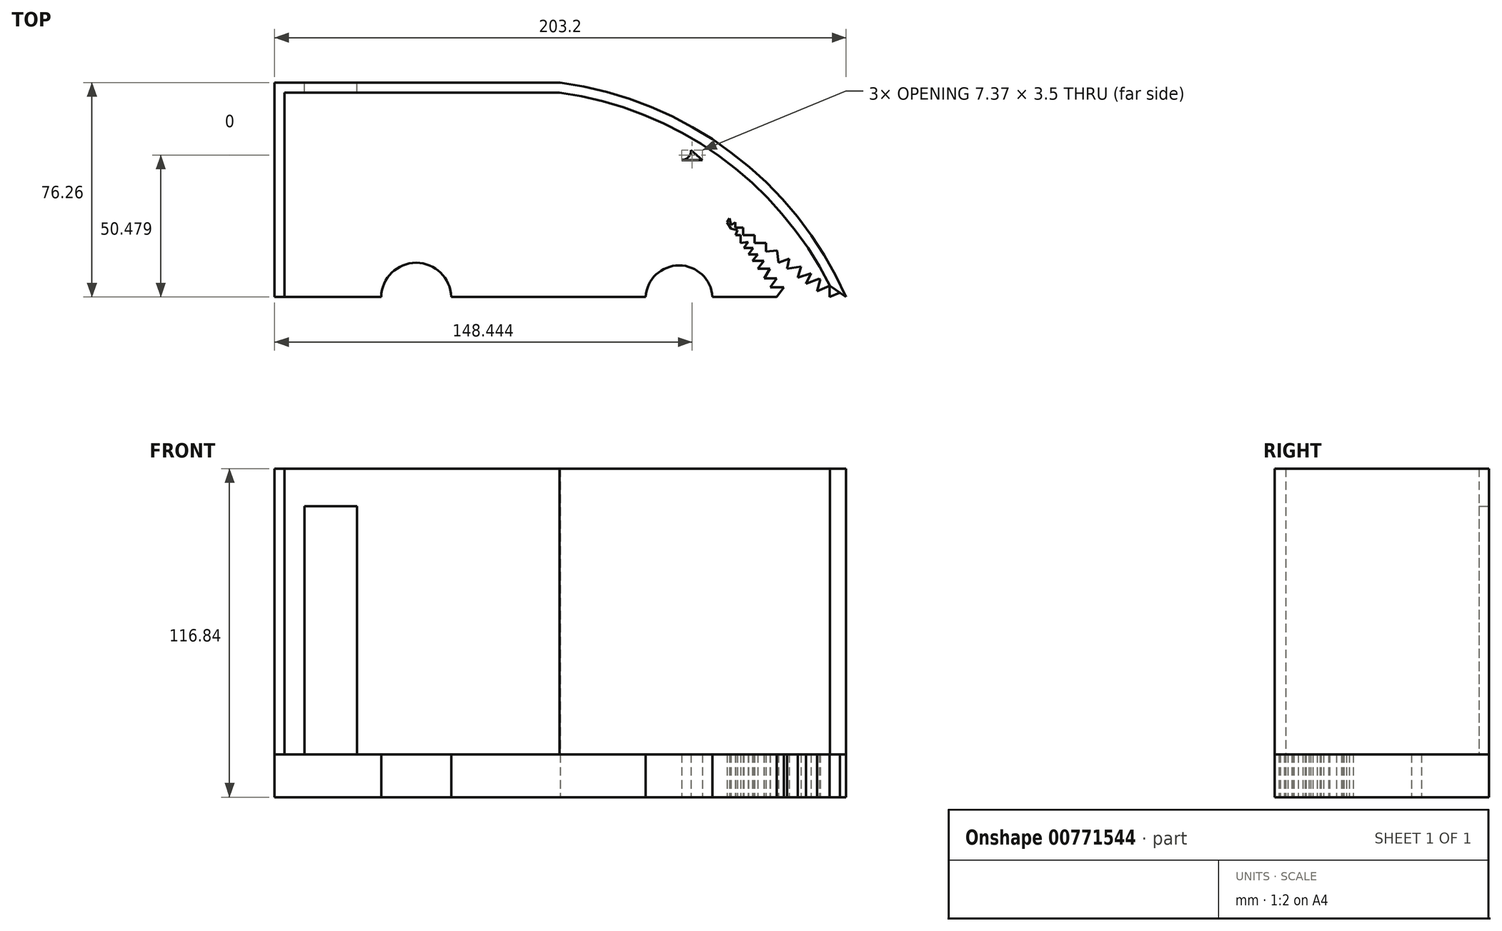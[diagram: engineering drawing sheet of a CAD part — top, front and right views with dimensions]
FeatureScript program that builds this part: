
annotation { "Feature Type Name" : "Feature", "Feature Type Description" : "" }
export const myFeature = defineFeature(function(context is Context, id is Id, definition is map)
    precondition{}
    {
        {
            var Q0;
            Q0=qCreatedBy(makeId("Top.planeOp"),FACE);
            var sketch = newSketch(context, id + "F0", { "sketchPlane" : qUnion([Q0])});
            skLineSegment(sketch, "E0.bottom", {"start": v(-120.33, 46.06) * mm, "end": v(-18.73, 46.06) * mm});
            skLineSegment(sketch, "E0.top", {"start": v(-120.33, -30.14) * mm, "end": v(-82.43, -30.14) * mm});
            skLineSegment(sketch, "E0.left", {"start": v(-120.33, 46.06) * mm, "end": v(-120.33, -30.14) * mm});
            skArc(sketch, "E1", {"start": v(82.87, -30.14) * mm, "mid": v(42, 21.2) * mm, "end": v(-18.73, 46.06) * mm});
            skLineSegment(sketch, "E2", {"start": v(40.49, -3.62) * mm, "end": v(41.97, -5.85) * mm});
            skLineSegment(sketch, "E3", {"start": v(27.75, 22.03) * mm, "end": v(31.8, 18.53) * mm});
            skLineSegment(sketch, "E4", {"start": v(31.8, 18.53) * mm, "end": v(24.43, 18.53) * mm});
            skLineSegment(sketch, "E5", {"start": v(24.43, 18.53) * mm, "end": v(31.8, 18.53) * mm});
            skPoint(sketch, "E6", {"position": v(31.8, 18.53) * mm});
            skArc(sketch, "E7", {"start": v(35.38, -30.14) * mm, "mid": v(23.48, -18.95) * mm, "end": v(11.6, -30.14) * mm});
            skLineSegment(sketch, "E8.trimOffspring", {"start": v(35.38, -30.14) * mm, "end": v(58.16, -30.14) * mm});
            skArc(sketch, "E9", {"start": v(-57.54, -30.14) * mm, "mid": v(-69.98, -18.02) * mm, "end": v(-82.43, -30.14) * mm});
            skLineSegment(sketch, "E10.trimOffspring", {"start": v(-57.54, -30.14) * mm, "end": v(11.6, -30.14) * mm});
            skPoint(sketch, "E11.orphan", {"position": v(82.87, 46.06) * mm});
            skPoint(sketch, "E12.end.orphan", {"position": v(-18.73, -30.14) * mm});
            skArc(sketch, "E13", {"start": v(24.43, 18.53) * mm, "mid": v(26.84, 19.57) * mm, "end": v(27.75, 22.03) * mm});
            skPoint(sketch, "E14.end.orphan", {"position": v(48.45, -15.57) * mm});
            skPoint(sketch, "E15.end.orphan", {"position": v(48.45, -6.99) * mm});
            skLineSegment(sketch, "E16", {"start": v(43.46, -3.62) * mm, "end": v(43.46, -5.5) * mm});
            skLineSegment(sketch, "E17", {"start": v(43.46, -5.5) * mm, "end": v(46.24, -5.5) * mm});
            skLineSegment(sketch, "E18", {"start": v(46.24, -5.5) * mm, "end": v(46.24, -8.2) * mm});
            skLineSegment(sketch, "E19", {"start": v(46.24, -8.2) * mm, "end": v(50.26, -8.2) * mm});
            skLineSegment(sketch, "E20", {"start": v(50.26, -8.2) * mm, "end": v(50.26, -11) * mm});
            skLineSegment(sketch, "E21", {"start": v(50.26, -11) * mm, "end": v(54.42, -11) * mm});
            skLineSegment(sketch, "E22", {"start": v(54.42, -11) * mm, "end": v(54.42, -14.07) * mm});
            skLineSegment(sketch, "E23", {"start": v(54.42, -14.07) * mm, "end": v(58.33, -13.63) * mm});
            skLineSegment(sketch, "E24", {"start": v(58.33, -13.63) * mm, "end": v(58.82, -18) * mm});
            skLineSegment(sketch, "E25", {"start": v(58.82, -18) * mm, "end": v(62.64, -16.53) * mm});
            skLineSegment(sketch, "E26", {"start": v(62.64, -16.53) * mm, "end": v(61.86, -20.13) * mm});
            skLineSegment(sketch, "E27", {"start": v(61.86, -20.13) * mm, "end": v(66.77, -19.31) * mm});
            skLineSegment(sketch, "E28", {"start": v(66.77, -19.31) * mm, "end": v(65.68, -23.3) * mm});
            skLineSegment(sketch, "E29", {"start": v(65.68, -23.3) * mm, "end": v(70.37, -21.73) * mm});
            skLineSegment(sketch, "E30", {"start": v(70.37, -21.73) * mm, "end": v(68.65, -25.44) * mm});
            skLineSegment(sketch, "E31", {"start": v(68.65, -25.44) * mm, "end": v(73.26, -23.68) * mm});
            skLineSegment(sketch, "E32", {"start": v(73.74, -24) * mm, "end": v(72.6, -28.12) * mm});
            skLineSegment(sketch, "E33", {"start": v(72.6, -28.12) * mm, "end": v(77.04, -26.22) * mm});
            skLineSegment(sketch, "E34", {"start": v(77.04, -26.22) * mm, "end": v(77.04, -30.2) * mm});
            skLineSegment(sketch, "E35", {"start": v(77.04, -30.2) * mm, "end": v(80.65, -28.65) * mm});
            skLineSegment(sketch, "E36", {"start": v(58.16, -30.14) * mm, "end": v(60.75, -26.67) * mm});
            skLineSegment(sketch, "E37", {"start": v(60.75, -26.67) * mm, "end": v(55.85, -26.67) * mm});
            skLineSegment(sketch, "E38", {"start": v(55.85, -26.67) * mm, "end": v(58.16, -23.51) * mm});
            skLineSegment(sketch, "E39", {"start": v(58.16, -23.51) * mm, "end": v(53.75, -23.51) * mm});
            skLineSegment(sketch, "E40", {"start": v(53.75, -23.51) * mm, "end": v(55.72, -20.09) * mm});
            skLineSegment(sketch, "E41", {"start": v(55.72, -20.09) * mm, "end": v(51.46, -20.09) * mm});
            skLineSegment(sketch, "E42", {"start": v(51.46, -20.09) * mm, "end": v(53.58, -17.3) * mm});
            skLineSegment(sketch, "E43", {"start": v(53.58, -17.3) * mm, "end": v(49.6, -17.3) * mm});
            skLineSegment(sketch, "E44", {"start": v(49.6, -17.3) * mm, "end": v(51.46, -15.07) * mm});
            skPoint(sketch, "E44.endSnap0", {"position": v(48.12, -15.07) * mm});
            skLineSegment(sketch, "E45", {"start": v(51.46, -15.07) * mm, "end": v(48.12, -15.07) * mm});
            skLineSegment(sketch, "E46", {"start": v(48.12, -15.07) * mm, "end": v(49.77, -12.75) * mm});
            skLineSegment(sketch, "E47", {"start": v(49.77, -12.75) * mm, "end": v(46.57, -12.75) * mm});
            skLineSegment(sketch, "E48", {"start": v(46.57, -12.75) * mm, "end": v(48.05, -10.55) * mm});
            skLineSegment(sketch, "E49", {"start": v(48.05, -10.55) * mm, "end": v(45.37, -10.96) * mm});
            skLineSegment(sketch, "E50", {"start": v(45.37, -10.96) * mm, "end": v(45.37, -8.2) * mm});
            skLineSegment(sketch, "E51", {"start": v(45.37, -8.2) * mm, "end": v(43.54, -8.2) * mm});
            skLineSegment(sketch, "E52", {"start": v(41.97, -5.85) * mm, "end": v(44.19, -6.44) * mm});
            skPoint(sketch, "E52.startSnap0", {"position": v(41.97, -3.62) * mm});
            skLineSegment(sketch, "E53", {"start": v(44.19, -6.44) * mm, "end": v(43.54, -8.2) * mm});
            skPoint(sketch, "E54.orphan", {"position": v(40.49, -3.62) * mm});
            skLineSegment(sketch, "E55", {"start": v(43.46, -3.62) * mm, "end": v(41.97, -4.61) * mm});
            skLineSegment(sketch, "E56", {"start": v(41.97, -4.61) * mm, "end": v(41.45, -2.27) * mm});
            skLineSegment(sketch, "E57", {"start": v(41.45, -2.27) * mm, "end": v(40.49, -3.62) * mm});
            skLineSegment(sketch, "E58.trimOffspring", {"start": v(48.12, -15.07) * mm, "end": v(48.45, -15.57) * mm});
            skPoint(sketch, "E59.start.orphan", {"position": v(38.07, 0) * mm});
            skLineSegment(sketch, "E60.trimOffspring", {"start": v(73.26, -23.68) * mm, "end": v(73.74, -24) * mm});
            skLineSegment(sketch, "E61.trimOffspring", {"start": v(80.65, -28.65) * mm, "end": v(82.87, -30.14) * mm});
            skSolve(sketch);
        }
        {
            var Q0;
            Q0 = qSketchRegion(id + "F0", true);
            extrude(context, id + "F1", {"entities" : qUnion([Q0]), "depth" : 15.24 * mm, "offsetDistance" : 25.4 * mm});
        }
        {
            var Q0;
            Q0=makeQuery(id+"F1.opExtrude","CAP_FACE",FACE,{"disambiguationData":[OSD([sQuery(id+"F0.wireOp",EDGE,"E0.bottom"),sQuery(id+"F0.wireOp",EDGE,"E0.top"),sQuery(id+"F0.wireOp",EDGE,"E0.left"),sQuery(id+"F0.wireOp",EDGE,"E1"),sQuery(id+"F0.wireOp",EDGE,"E2"),sQuery(id+"F0.wireOp",EDGE,"E3"),sQuery(id+"F0.wireOp",EDGE,"E5"),sQuery(id+"F0.wireOp",EDGE,"E7"),sQuery(id+"F0.wireOp",EDGE,"E8.trimOffspring"),sQuery(id+"F0.wireOp",EDGE,"E9"),sQuery(id+"F0.wireOp",EDGE,"E10.trimOffspring"),sQuery(id+"F0.wireOp",EDGE,"E13"),sQuery(id+"F0.wireOp",EDGE,"E16"),sQuery(id+"F0.wireOp",EDGE,"E17"),sQuery(id+"F0.wireOp",EDGE,"E18"),sQuery(id+"F0.wireOp",EDGE,"E19"),sQuery(id+"F0.wireOp",EDGE,"E20"),sQuery(id+"F0.wireOp",EDGE,"E21"),sQuery(id+"F0.wireOp",EDGE,"E22"),sQuery(id+"F0.wireOp",EDGE,"E23"),sQuery(id+"F0.wireOp",EDGE,"E24"),sQuery(id+"F0.wireOp",EDGE,"E25"),sQuery(id+"F0.wireOp",EDGE,"E26"),sQuery(id+"F0.wireOp",EDGE,"E27"),sQuery(id+"F0.wireOp",EDGE,"E28"),sQuery(id+"F0.wireOp",EDGE,"E29"),sQuery(id+"F0.wireOp",EDGE,"E30"),sQuery(id+"F0.wireOp",EDGE,"E31"),sQuery(id+"F0.wireOp",EDGE,"E32"),sQuery(id+"F0.wireOp",EDGE,"E33"),sQuery(id+"F0.wireOp",EDGE,"E34"),sQuery(id+"F0.wireOp",EDGE,"E35"),sQuery(id+"F0.wireOp",EDGE,"E36"),sQuery(id+"F0.wireOp",EDGE,"E37"),sQuery(id+"F0.wireOp",EDGE,"E38"),sQuery(id+"F0.wireOp",EDGE,"E39"),sQuery(id+"F0.wireOp",EDGE,"E40"),sQuery(id+"F0.wireOp",EDGE,"E41"),sQuery(id+"F0.wireOp",EDGE,"E42"),sQuery(id+"F0.wireOp",EDGE,"E43"),sQuery(id+"F0.wireOp",EDGE,"E44"),sQuery(id+"F0.wireOp",EDGE,"E45"),sQuery(id+"F0.wireOp",EDGE,"E46"),sQuery(id+"F0.wireOp",EDGE,"E47"),sQuery(id+"F0.wireOp",EDGE,"E48"),sQuery(id+"F0.wireOp",EDGE,"E49"),sQuery(id+"F0.wireOp",EDGE,"E50"),sQuery(id+"F0.wireOp",EDGE,"E51"),sQuery(id+"F0.wireOp",EDGE,"E52"),sQuery(id+"F0.wireOp",EDGE,"E53"),sQuery(id+"F0.wireOp",EDGE,"E55"),sQuery(id+"F0.wireOp",EDGE,"E56"),sQuery(id+"F0.wireOp",EDGE,"E57"),sQuery(id+"F0.wireOp",EDGE,"E60.trimOffspring"),sQuery(id+"F0.wireOp",EDGE,"E61.trimOffspring")])],"isStart":false});
            var sketch = newSketch(context, id + "F2", { "sketchPlane" : qUnion([Q0])});
            skArc(sketch, "E62", {"start": v(82.87, -30.14) * mm, "mid": v(42, 21.2) * mm, "end": v(-18.73, 46.06) * mm});
            skPoint(sketch, "E62.first.point", {"position": v(-18.73, 46.06) * mm});
            skPoint(sketch, "E62.second.point", {"position": v(82.87, -30.14) * mm});
            skPoint(sketch, "E62.third.point", {"position": v(38.59, 23.67) * mm});
            skLineSegment(sketch, "E63", {"start": v(-18.73, 46.06) * mm, "end": v(-120.33, 46.06) * mm});
            skLineSegment(sketch, "E64", {"start": v(-120.33, 46.06) * mm, "end": v(-120.33, -30.14) * mm});
            skLineSegment(sketch, "E65.0", {"start": v(-116.78, 42.5) * mm, "end": v(-116.78, -30.14) * mm});
            skLineSegment(sketch, "E65.1", {"start": v(-18.97, 42.5) * mm, "end": v(-116.78, 42.5) * mm});
            skArc(sketch, "E65.2", {"start": v(77.11, -26.27) * mm, "mid": v(37.6, 20.02) * mm, "end": v(-18.97, 42.5) * mm});
            skLineSegment(sketch, "E66", {"start": v(-116.78, -30.14) * mm, "end": v(-120.33, -30.14) * mm});
            skLineSegment(sketch, "E67", {"start": v(82.87, -30.14) * mm, "end": v(77.04, -26.22) * mm});
            skSolve(sketch);
        }
        {
            var Q0;
            Q0 = qSketchRegion(id + "F2", true);
            extrude(context, id + "F3", {"entities" : qUnion([Q0]), "depth" : 101.6 * mm, "offsetDistance" : 25.4 * mm});
        }
        {
            var Q0;
            Q0=makeQuery(id+"F3.opExtrude","SWEPT_FACE",FACE,{"disambiguationData":[OSD([sQuery(id+"F2.wireOp",EDGE,"E63")])]});
            var sketch = newSketch(context, id + "F4", { "sketchPlane" : qUnion([Q0])});
            skLineSegment(sketch, "E68.bottom", {"start": v(109.72, 15.24) * mm, "end": v(91, 15.24) * mm});
            skLineSegment(sketch, "E68.top", {"start": v(109.72, 103.43) * mm, "end": v(91, 103.43) * mm});
            skLineSegment(sketch, "E68.left", {"start": v(109.72, 15.24) * mm, "end": v(109.72, 103.43) * mm});
            skLineSegment(sketch, "E68.right", {"start": v(91, 15.24) * mm, "end": v(91, 103.43) * mm});
            skSolve(sketch);
        }
        {
            var Q0;
            Q0 = qSketchRegion(id + "F4", true);
            extrude(context, id + "F5", {"entities" : qUnion([Q0]), "operationType" : NewBodyOperationType.REMOVE, "oppositeDirection" : true, "depth" : 25.4 * mm, "offsetDistance" : 25.4 * mm});
        }
    });
